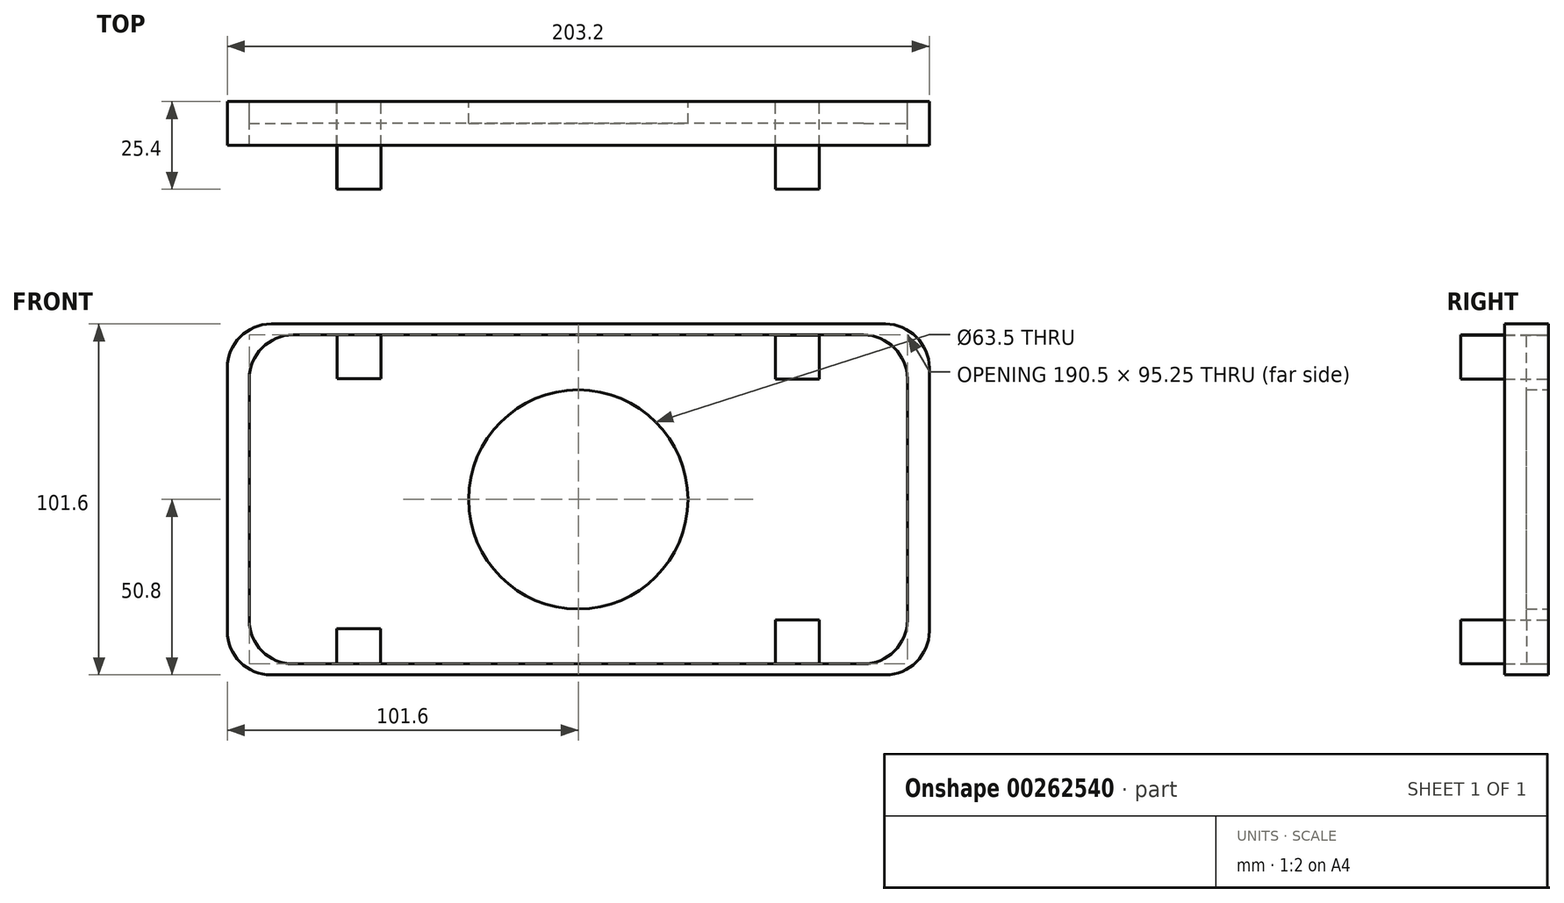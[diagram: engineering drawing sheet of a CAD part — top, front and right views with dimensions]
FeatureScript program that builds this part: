
annotation { "Feature Type Name" : "Feature", "Feature Type Description" : "" }
export const myFeature = defineFeature(function(context is Context, id is Id, definition is map)
    precondition{}
    {
        {
            var Q0;
            Q0=qCreatedBy(makeId("Front.planeOp"),FACE);
            var sketch = newSketch(context, id + "F0", { "sketchPlane" : qUnion([Q0])});
            skLineSegment(sketch, "E0.bottom", {"start": v(88.9, -50.8) * mm, "end": v(-88.9, -50.8) * mm});
            skLineSegment(sketch, "E0.top", {"start": v(88.9, 50.8) * mm, "end": v(-88.9, 50.8) * mm});
            skLineSegment(sketch, "E0.left", {"start": v(101.6, -38.1) * mm, "end": v(101.6, 38.1) * mm});
            skLineSegment(sketch, "E0.right", {"start": v(-101.6, -38.1) * mm, "end": v(-101.6, 38.1) * mm});
            skPoint(sketch, "E0.middle", {"position": v(0, 0) * mm});
            skLineSegment(sketch, "E1.bottom", {"start": v(82.55, -47.62) * mm, "end": v(-82.55, -47.63) * mm});
            skLineSegment(sketch, "E1.top", {"start": v(82.55, 47.63) * mm, "end": v(-82.55, 47.63) * mm});
            skLineSegment(sketch, "E1.left", {"start": v(95.25, -34.92) * mm, "end": v(95.25, 34.93) * mm});
            skLineSegment(sketch, "E1.right", {"start": v(-95.25, -34.93) * mm, "end": v(-95.25, 34.92) * mm});
            skPoint(sketch, "E2.visualSharp", {"position": v(-95.25, 47.62) * mm});
            skArc(sketch, "E2.filletArc", {"start": v(-82.55, 47.63) * mm, "mid": v(-91.53, 43.9) * mm, "end": v(-95.25, 34.92) * mm});
            skPoint(sketch, "E3.visualSharp", {"position": v(-101.6, 50.8) * mm});
            skArc(sketch, "E3.filletArc", {"start": v(-88.9, 50.8) * mm, "mid": v(-97.88, 47.08) * mm, "end": v(-101.6, 38.1) * mm});
            skPoint(sketch, "E4.visualSharp", {"position": v(95.25, 47.63) * mm});
            skArc(sketch, "E4.filletArc", {"start": v(95.25, 34.93) * mm, "mid": v(91.53, 43.9) * mm, "end": v(82.55, 47.63) * mm});
            skPoint(sketch, "E5.visualSharp", {"position": v(101.6, 50.8) * mm});
            skArc(sketch, "E5.filletArc", {"start": v(101.6, 38.1) * mm, "mid": v(97.88, 47.08) * mm, "end": v(88.9, 50.8) * mm});
            skPoint(sketch, "E6.visualSharp", {"position": v(95.25, -47.62) * mm});
            skArc(sketch, "E6.filletArc", {"start": v(82.55, -47.62) * mm, "mid": v(91.53, -43.9) * mm, "end": v(95.25, -34.92) * mm});
            skPoint(sketch, "E7.visualSharp", {"position": v(101.6, -50.8) * mm});
            skArc(sketch, "E7.filletArc", {"start": v(88.9, -50.8) * mm, "mid": v(97.88, -47.08) * mm, "end": v(101.6, -38.1) * mm});
            skPoint(sketch, "E8.visualSharp", {"position": v(-101.6, -50.8) * mm});
            skArc(sketch, "E8.filletArc", {"start": v(-101.6, -38.1) * mm, "mid": v(-97.88, -47.08) * mm, "end": v(-88.9, -50.8) * mm});
            skPoint(sketch, "E9.visualSharp", {"position": v(-95.25, -47.63) * mm});
            skArc(sketch, "E9.filletArc", {"start": v(-95.25, -34.93) * mm, "mid": v(-91.53, -43.9) * mm, "end": v(-82.55, -47.63) * mm});
            skLineSegment(sketch, "E10", {"start": v(0, 47.63) * mm, "end": v(0, -47.62) * mm});
            skCircle(sketch, "E11", {"center": v(0, 0) * mm, "radius": 31.75 * mm});
            skSolve(sketch);
        }
        {
            var Q0;
            Q0=makeQuery(id+"F0.imprint","IMPRINT",FACE,{"disambiguationData":[TD([[makeQuery(id+"F0.imprint","IMPRINT",EDGE,{"derivedFrom":sQuery(id+"F0.wireOp",EDGE,"E1.bottom")}),-1.0]])]});
            extrude(context, id + "F1", {"entities" : qUnion([Q0]), "depth" : 6.35 * mm});
        }
        {
            var Q0;
            Q0=makeQuery(id+"F0.imprint","IMPRINT",FACE,{"disambiguationData":[TD([[makeQuery(id+"F0.imprint","IMPRINT",EDGE,{"derivedFrom":sQuery(id+"F0.wireOp",EDGE,"E0.bottom")}),-1.0]])]});
            extrude(context, id + "F2", {"entities" : qUnion([Q0]), "depth" : 12.7 * mm});
        }
        {
            var Q0;
            {var subQ0=sQuery(id+"F0.wireOp",EDGE,"E11");var subQ1=sQuery(id+"F0.wireOp",EDGE,"E10");var subQ2=makeQuery(id+"F0.imprint","INTERSECT",VERTEX,{"disambiguationData":[OD(0.0)],"derivedFrom":[subQ1,subQ0]});Q0=makeQuery(id+"F0.imprint","IMPRINT",FACE,{"disambiguationData":[TD([[makeQuery(id+"F0.imprint","IMPRINT",EDGE,{"disambiguationData":[TD([[subQ2,-1.0]])],"derivedFrom":subQ1}),-1.0]])]});}
            var Q1;
            {var subQ0=sQuery(id+"F0.wireOp",EDGE,"E11");var subQ1=sQuery(id+"F0.wireOp",EDGE,"E10");var subQ2=makeQuery(id+"F0.imprint","INTERSECT",VERTEX,{"disambiguationData":[OD(0.0)],"derivedFrom":[subQ1,subQ0]});Q1=makeQuery(id+"F0.imprint","IMPRINT",FACE,{"disambiguationData":[TD([[makeQuery(id+"F0.imprint","IMPRINT",EDGE,{"disambiguationData":[TD([[subQ2,-1.0]])],"derivedFrom":subQ1}),1.0]])]});}
            extrude(context, id + "F3", {"entities" : qUnion([Q0, Q1]), "depth" : 6.35 * mm});
        }
        {
            var Q0;
            Q0=makeQuery(id+"F0.imprint","IMPRINT",FACE,{"disambiguationData":[TD([[makeQuery(id+"F0.imprint","IMPRINT",EDGE,{"derivedFrom":sQuery(id+"F0.wireOp",EDGE,"E1.right")}),-1.0]])]});
            var sketch = newSketch(context, id + "F4", { "sketchPlane" : qUnion([Q0])});
            skLineSegment(sketch, "E12", {"start": v(-82.66, -47.72) * mm, "end": v(-69.96, -47.72) * mm});
            skLineSegment(sketch, "E13.bottom", {"start": v(-69.96, -47.72) * mm, "end": v(-57.26, -47.72) * mm});
            skLineSegment(sketch, "E13.top", {"start": v(-69.96, -37.35) * mm, "end": v(-57.26, -37.35) * mm});
            skLineSegment(sketch, "E13.left", {"start": v(-69.96, -47.72) * mm, "end": v(-69.96, -37.35) * mm});
            skLineSegment(sketch, "E13.right", {"start": v(-57.26, -47.72) * mm, "end": v(-57.26, -37.35) * mm});
            skLineSegment(sketch, "E14", {"start": v(82.44, -47.62) * mm, "end": v(69.74, -47.62) * mm});
            skLineSegment(sketch, "E15.bottom", {"start": v(69.74, -47.62) * mm, "end": v(57.04, -47.62) * mm});
            skLineSegment(sketch, "E15.top", {"start": v(69.74, -34.92) * mm, "end": v(57.04, -34.92) * mm});
            skLineSegment(sketch, "E15.left", {"start": v(69.74, -47.62) * mm, "end": v(69.74, -34.92) * mm});
            skLineSegment(sketch, "E15.right", {"start": v(57.04, -47.62) * mm, "end": v(57.04, -34.92) * mm});
            skLineSegment(sketch, "E16", {"start": v(82.53, 47.6) * mm, "end": v(69.84, 47.6) * mm});
            skLineSegment(sketch, "E17.bottom", {"start": v(69.84, 47.6) * mm, "end": v(57.14, 47.6) * mm});
            skLineSegment(sketch, "E17.top", {"start": v(69.84, 34.9) * mm, "end": v(57.14, 34.9) * mm});
            skLineSegment(sketch, "E17.left", {"start": v(69.84, 47.6) * mm, "end": v(69.84, 34.9) * mm});
            skLineSegment(sketch, "E17.right", {"start": v(57.14, 47.6) * mm, "end": v(57.14, 34.9) * mm});
            skLineSegment(sketch, "E18", {"start": v(-82.55, 47.62) * mm, "end": v(-69.85, 47.62) * mm});
            skLineSegment(sketch, "E19.bottom", {"start": v(-69.85, 47.62) * mm, "end": v(-57.15, 47.62) * mm});
            skLineSegment(sketch, "E19.top", {"start": v(-69.85, 34.92) * mm, "end": v(-57.15, 34.92) * mm});
            skLineSegment(sketch, "E19.left", {"start": v(-69.85, 47.62) * mm, "end": v(-69.85, 34.92) * mm});
            skLineSegment(sketch, "E19.right", {"start": v(-57.15, 47.62) * mm, "end": v(-57.15, 34.92) * mm});
            skSolve(sketch);
        }
        {
            var Q0;
            {var subQ0=sQuery(id+"F4.wireOp",EDGE,"E13.top");Q0=makeQuery(id+"F4.imprint","IMPRINT",FACE,{"disambiguationData":[TD([[makeQuery(id+"F4.imprint","IMPRINT",EDGE,{"derivedFrom":subQ0}),-1.0]])]});}
            var Q1;
            Q1=makeQuery(id+"F4.imprint","IMPRINT",FACE,{"disambiguationData":[TD([[makeQuery(id+"F4.imprint","IMPRINT",EDGE,{"derivedFrom":sQuery(id+"F4.wireOp",EDGE,"E17.bottom")}),1.0]])]});
            var Q2;
            Q2=makeQuery(id+"F4.imprint","IMPRINT",FACE,{"disambiguationData":[TD([[makeQuery(id+"F4.imprint","IMPRINT",EDGE,{"derivedFrom":sQuery(id+"F4.wireOp",EDGE,"E15.bottom")}),-1.0]])]});
            var Q3;
            Q3=makeQuery(id+"F4.imprint","IMPRINT",FACE,{"disambiguationData":[TD([[makeQuery(id+"F4.imprint","IMPRINT",EDGE,{"derivedFrom":sQuery(id+"F4.wireOp",EDGE,"E19.bottom")}),-1.0]])]});
            extrude(context, id + "F5", {"entities" : qUnion([Q0, Q1, Q2, Q3]), "depth" : 25.4 * mm});
        }
    });
